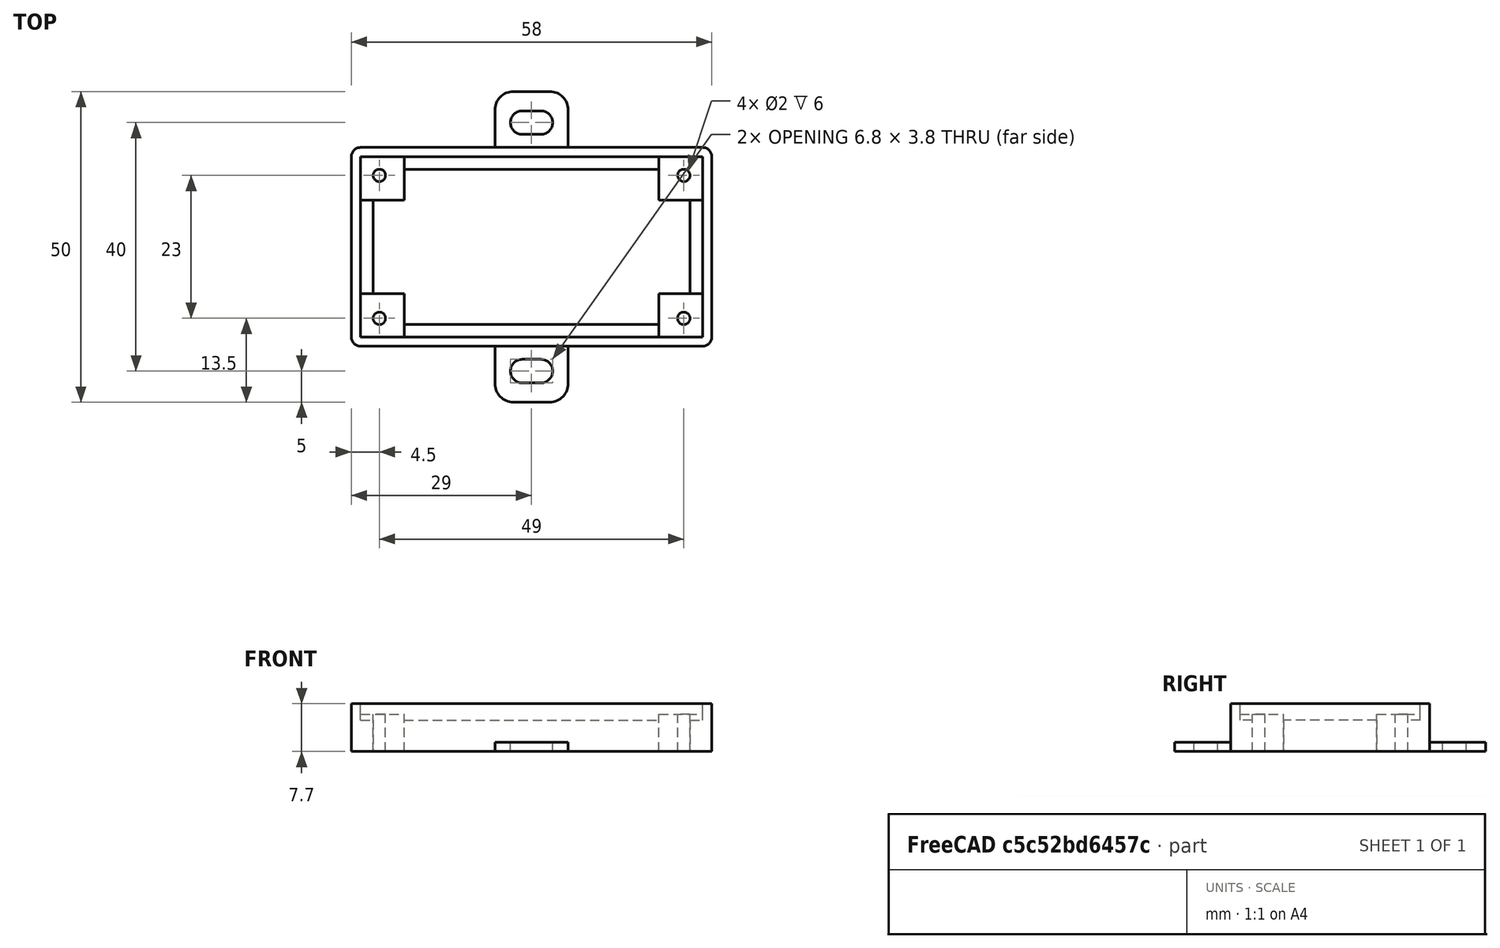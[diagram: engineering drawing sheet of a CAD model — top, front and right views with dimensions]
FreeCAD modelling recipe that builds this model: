
FCSTD DOCUMENT  (FreeCAD 0.19R23578 (Git))
Label: stepper_driver_cjmcu_vnh2sp30
License: All rights reserved
LicenseURL: http://en.wikipedia.org/wiki/All_rights_reserved
objects: Part::Box×4, Part::MultiFuse×3, Part::FeaturePython×2, Part::Cut×2, Spreadsheet::Sheet×1, Part::Cylinder×1, Part::Fillet×1, Part::Feature×1, App::Part×1
note: 14 computed .brp shape members not serialized (recipe doc carries the construction recipe); baked Part::Feature solids carry a one-line shape summary decoded from their .brp

FEATURE [Spreadsheet::Sheet] Spreadsheet  label="p"
  cells = A1=hole_x_dist; B1(hole_x_dist)=49; A2=hole_y_dist; B2(hole_y_dist)=23; A3=pcb_under; B3(pcb_under)=3; A4=pcb_x; B4(pcb_x)=55; A5=pcb_y; B5(pcb_y)=29; A6=hole_stand_x; B6(hole_stand_x)=7; A7=hole_stand_y; B7(hole_stand_y)=7; A8=hole_r; B8(hole_r)=1; A9=box_wall; B9(box_wall)=1.5; A10=under_layer; B10(under_layer)=3; A11=pcb_height; B11(pcb_height)=1.7; A12=under_pcb_border; B12(under_pcb_border)=2
FEATURE [Part::Box] Box  label="bottom cube"
  AttacherType = Attacher::AttachEngine3D
  Height = 7.7
  Length = 58
  Width = 32
  expr: Width = <<p>>.pcb_y + <<p>>.box_wall * 2
  expr: Length = <<p>>.pcb_x + <<p>>.box_wall * 2
  expr: Height = <<p>>.pcb_under + <<p>>.pcb_height + <<p>>.under_layer
FEATURE [Part::Box] Box001  label="bottom extraction"
  AttacherType = Attacher::AttachEngine3D
  Height = 10
  Length = 51
  Placement = pos=(3.5,3.5,0) rot=(0,0,1;0rad)
  Width = 25
  expr: .Placement.Base.y = <<p>>.under_pcb_border + <<p>>.box_wall
  expr: .Placement.Base.x = <<p>>.under_pcb_border + <<p>>.box_wall
  expr: Length = <<p>>.pcb_x - <<p>>.under_pcb_border * 2
  expr: Width = <<p>>.pcb_y - <<p>>.under_pcb_border * 2
FEATURE [Part::Box] Box002  label="pcb extraction"
  AttacherType = Attacher::AttachEngine3D
  Height = 10
  Length = 55
  Placement = pos=(1.5,1.5,5) rot=(0,0,1;0rad)
  Width = 29
  expr: .Placement.Base.z = <<p>>.under_pcb_border + <<p>>.under_layer
  expr: .Placement.Base.y = <<p>>.box_wall
  expr: .Placement.Base.x = <<p>>.box_wall
  expr: Length = <<p>>.pcb_x
  expr: Width = <<p>>.pcb_y
FEATURE [Part::MultiFuse] Fusion  label="bottom extraction001"
  Shapes = -> [Box001,Box002]
FEATURE [Part::Box] Box003  label="hole stand cube"
  AttacherType = Attacher::AttachEngine3D
  Height = 6
  Length = 7
  Placement = pos=(1.5,1.5,0) rot=(0,0,1;0rad)
  Width = 7
  expr: .Placement.Base.y = <<p>>.box_wall
  expr: .Placement.Base.x = <<p>>.box_wall
  expr: Height = <<p>>.pcb_under + <<p>>.under_layer
  expr: Width = <<p>>.hole_stand_y
  expr: Length = <<p>>.hole_stand_x
FEATURE [Part::FeaturePython] Array  label="hole stand array"  # Draft array (typed FeaturePython)
  Angle = 360
  ArrayType = 0
  Axis = (0,0,1)
  Base = -> Box003
  Center = (0,0,0)
  Fuse = false
  IntervalAxis = (0,0,0)
  IntervalX = (48,0,0)
  IntervalY = (0,22,0)
  IntervalZ = (0,0,1)
  NumberPolar = 1
  NumberX = 2
  NumberY = 2
  NumberZ = 1
  expr: .IntervalY.y = <<p>>.pcb_y - <<p>>.hole_stand_y
  expr: .IntervalX.x = <<p>>.pcb_x - <<p>>.hole_stand_x
FEATURE [Part::Cylinder] Cylinder  label="pcb hole"
  Angle = 360
  AttacherType = Attacher::AttachEngine3D
  Height = 10
  Placement = pos=(4.5,4.5,0) rot=(0,0,1;0rad)
  Radius = 1
  expr: .Placement.Base.y = (<<p>>.box_wall * 2 + <<p>>.pcb_y - <<p>>.hole_y_dist) / 2
  expr: .Placement.Base.x = (<<p>>.box_wall * 2 + <<p>>.pcb_x - <<p>>.hole_x_dist) / 2
  expr: Radius = <<p>>.hole_r
FEATURE [Part::FeaturePython] Array001  label="hole array"  # Draft array (typed FeaturePython)
  Angle = 360
  ArrayType = 0
  Axis = (0,0,1)
  Base = -> Cylinder
  Center = (0,0,0)
  Fuse = false
  IntervalAxis = (0,0,0)
  IntervalX = (49,0,0)
  IntervalY = (0,23,0)
  IntervalZ = (0,0,1)
  NumberPolar = 1
  NumberX = 2
  NumberY = 2
  NumberZ = 1
  expr: .IntervalY.y = <<p>>.hole_y_dist
  expr: .IntervalX.x = <<p>>.hole_x_dist
FEATURE [Part::Fillet] Fillet001  label="bottom cube fillet"
  Base = -> Box
  Edges = 4 edges r=1.5: [Edge1,Edge3,Edge5,Edge7]
FEATURE [Part::Feature] Cut002002  label="attach plane y dir002"
  Placement = pos=(23.1,-9,0) rot=(0,0,1;0rad)
  shape: bbox 11.8 x 50 x 1.5 mm, 20 faces (baked)
FEATURE [Part::MultiFuse] Fusion002  label="bottom fusion"
  Shapes = -> [Fillet001,Cut002002]
FEATURE [Part::Cut] Cut  label="pcb box cut"
  Base = -> Fusion002
  Tool = -> Fusion
FEATURE [Part::MultiFuse] Fusion001  label="frame fusion"
  Shapes = -> [Array,Cut]
FEATURE [Part::Cut] Cut001  label="frame fusion with holes"
  Base = -> Fusion001
  Tool = -> Array001
FEATURE [App::Part] Part  label="pcb with 4 holes part"
  Group = -> [Fusion,Fusion002,Box002,Box003,Box001,Array001,Box,Cut,Array,Cylinder,Fusion001,Cut001]
  Origin = -> Origin
